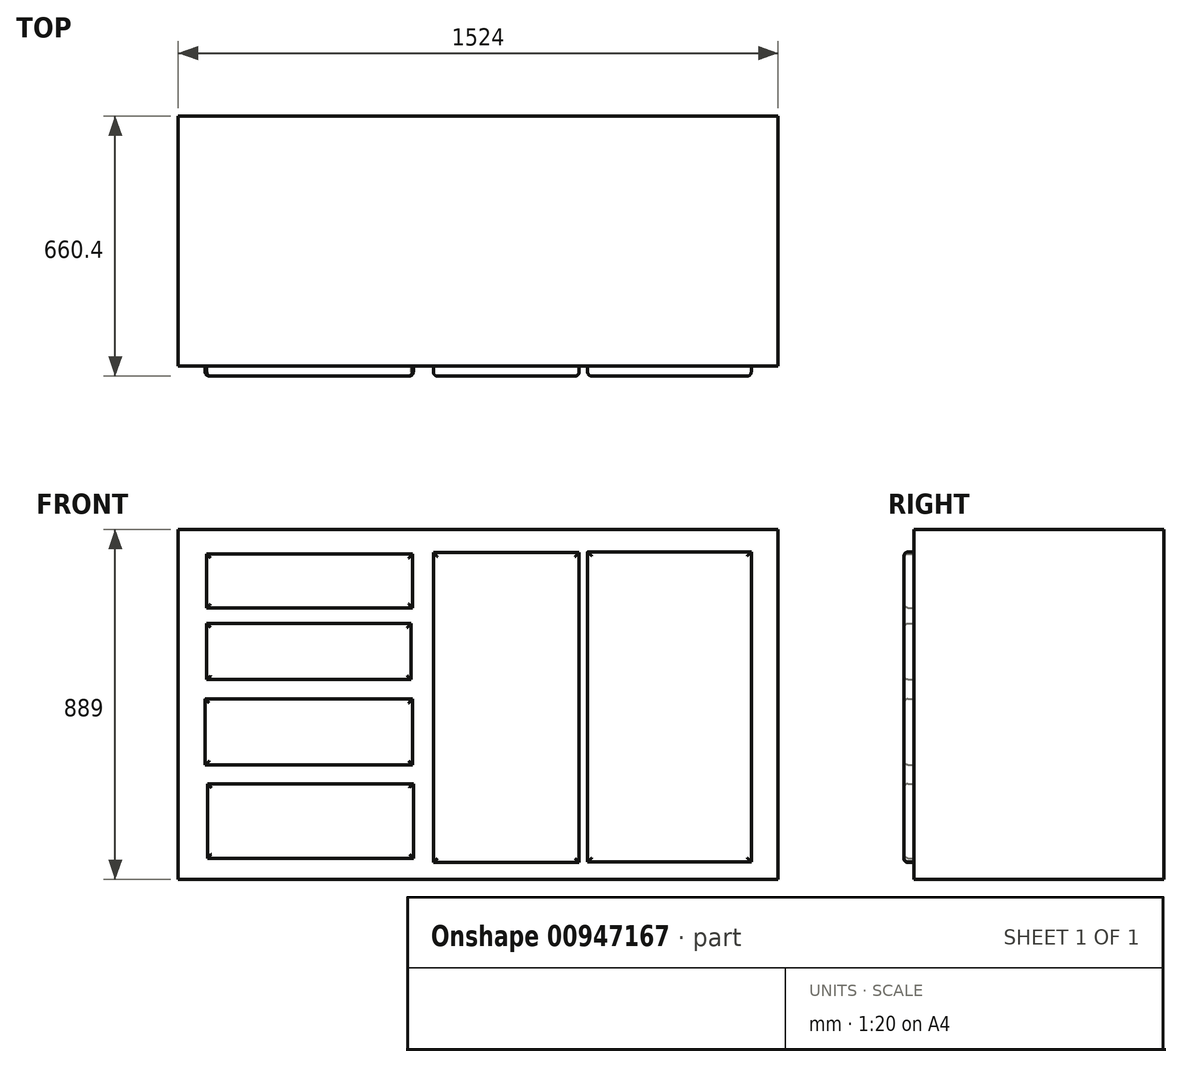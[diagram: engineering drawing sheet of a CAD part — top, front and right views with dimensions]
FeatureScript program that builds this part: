
annotation { "Feature Type Name" : "Feature", "Feature Type Description" : "" }
export const myFeature = defineFeature(function(context is Context, id is Id, definition is map)
    precondition{}
    {
        {
            var Q0;
            Q0=qCreatedBy(makeId("Top.planeOp"),FACE);
            var sketch = newSketch(context, id + "F0", { "sketchPlane" : qUnion([Q0])});
            skLineSegment(sketch, "E0.bottom", {"start": v(0, 0) * mm, "end": v(1524, 0) * mm});
            skLineSegment(sketch, "E0.top", {"start": v(0, 635) * mm, "end": v(1524, 635) * mm});
            skLineSegment(sketch, "E0.left", {"start": v(0, 0) * mm, "end": v(0, 635) * mm});
            skLineSegment(sketch, "E0.right", {"start": v(1524, 0) * mm, "end": v(1524, 635) * mm});
            skSolve(sketch);
        }
        {
            var Q0;
            Q0 = qSketchRegion(id + "F0", true);
            extrude(context, id + "F1", {"entities" : qUnion([Q0]), "depth" : 889 * mm, "offsetDistance" : 25.4 * mm});
        }
        {
            var Q0;
            Q0=makeQuery(id+"F1.opExtrude","SWEPT_FACE",FACE,{"disambiguationData":[OSD([sQuery(id+"F0.wireOp",EDGE,"E0.bottom")])]});
            var sketch = newSketch(context, id + "F2", { "sketchPlane" : qUnion([Q0])});
            skLineSegment(sketch, "E1.bottom", {"start": v(1455.74, 832.02) * mm, "end": v(1040.15, 832.02) * mm});
            skLineSegment(sketch, "E1.top", {"start": v(1455.74, 44.58) * mm, "end": v(1040.15, 44.58) * mm});
            skLineSegment(sketch, "E1.left", {"start": v(1455.74, 832.02) * mm, "end": v(1455.74, 44.58) * mm});
            skLineSegment(sketch, "E1.right", {"start": v(1040.15, 832.02) * mm, "end": v(1040.15, 44.58) * mm});
            skLineSegment(sketch, "E2.bottom", {"start": v(1018.28, 42.76) * mm, "end": v(648.26, 42.76) * mm});
            skLineSegment(sketch, "E2.top", {"start": v(1018.28, 830.2) * mm, "end": v(648.26, 830.2) * mm});
            skLineSegment(sketch, "E2.left", {"start": v(1018.28, 42.76) * mm, "end": v(1018.28, 830.2) * mm});
            skLineSegment(sketch, "E2.right", {"start": v(648.26, 42.76) * mm, "end": v(648.26, 830.2) * mm});
            skLineSegment(sketch, "E3.bottom", {"start": v(595.4, 826.55) * mm, "end": v(72.26, 826.55) * mm});
            skLineSegment(sketch, "E3.top", {"start": v(595.4, 689.84) * mm, "end": v(72.26, 689.84) * mm});
            skLineSegment(sketch, "E3.left", {"start": v(595.4, 826.55) * mm, "end": v(595.4, 689.84) * mm});
            skLineSegment(sketch, "E3.right", {"start": v(72.26, 826.55) * mm, "end": v(72.26, 689.84) * mm});
            skLineSegment(sketch, "E4.bottom", {"start": v(591.75, 649.74) * mm, "end": v(72.26, 649.74) * mm});
            skLineSegment(sketch, "E4.top", {"start": v(591.75, 507.56) * mm, "end": v(72.26, 507.56) * mm});
            skLineSegment(sketch, "E4.left", {"start": v(591.75, 649.74) * mm, "end": v(591.75, 507.56) * mm});
            skLineSegment(sketch, "E4.right", {"start": v(72.26, 649.74) * mm, "end": v(72.26, 507.56) * mm});
            skLineSegment(sketch, "E5.bottom", {"start": v(595.4, 458.35) * mm, "end": v(68.61, 458.35) * mm});
            skLineSegment(sketch, "E5.top", {"start": v(595.4, 290.65) * mm, "end": v(68.61, 290.65) * mm});
            skLineSegment(sketch, "E5.left", {"start": v(595.4, 458.35) * mm, "end": v(595.4, 290.65) * mm});
            skLineSegment(sketch, "E5.right", {"start": v(68.61, 458.35) * mm, "end": v(68.61, 290.65) * mm});
            skLineSegment(sketch, "E6.bottom", {"start": v(597.22, 243.26) * mm, "end": v(74.08, 243.26) * mm});
            skLineSegment(sketch, "E6.top", {"start": v(597.22, 53.7) * mm, "end": v(74.08, 53.7) * mm});
            skLineSegment(sketch, "E6.left", {"start": v(597.22, 243.26) * mm, "end": v(597.22, 53.7) * mm});
            skLineSegment(sketch, "E6.right", {"start": v(74.08, 243.26) * mm, "end": v(74.08, 53.7) * mm});
            skSolve(sketch);
        }
        {
            var Q0;
            Q0 = qSketchRegion(id + "F2", true);
            extrude(context, id + "F3", {"entities" : qUnion([Q0]), "operationType" : NewBodyOperationType.ADD, "depth" : 25.4 * mm, "offsetDistance" : 25.4 * mm});
        }
        {
            var Q0;
            Q0=makeQuery(id+"F3.opExtrude","CAP_FACE",FACE,{"disambiguationData":[OSD([sQuery(id+"F2.wireOp",EDGE,"E3.bottom"),sQuery(id+"F2.wireOp",EDGE,"E3.top"),sQuery(id+"F2.wireOp",EDGE,"E3.left"),sQuery(id+"F2.wireOp",EDGE,"E3.right")])],"isStart":false});
            var Q1;
            Q1=makeQuery(id+"F3.opExtrude","CAP_FACE",FACE,{"disambiguationData":[OSD([sQuery(id+"F2.wireOp",EDGE,"E2.bottom"),sQuery(id+"F2.wireOp",EDGE,"E2.top"),sQuery(id+"F2.wireOp",EDGE,"E2.left"),sQuery(id+"F2.wireOp",EDGE,"E2.right")])],"isStart":false});
            var Q2;
            Q2=makeQuery(id+"F3.opExtrude","CAP_FACE",FACE,{"disambiguationData":[OSD([sQuery(id+"F2.wireOp",EDGE,"E1.bottom"),sQuery(id+"F2.wireOp",EDGE,"E1.top"),sQuery(id+"F2.wireOp",EDGE,"E1.left"),sQuery(id+"F2.wireOp",EDGE,"E1.right")])],"isStart":false});
            var Q3;
            Q3=makeQuery(id+"F3.opExtrude","CAP_FACE",FACE,{"disambiguationData":[OSD([sQuery(id+"F2.wireOp",EDGE,"E4.bottom"),sQuery(id+"F2.wireOp",EDGE,"E4.top"),sQuery(id+"F2.wireOp",EDGE,"E4.left"),sQuery(id+"F2.wireOp",EDGE,"E4.right")])],"isStart":false});
            var Q4;
            Q4=makeQuery(id+"F3.opExtrude","CAP_FACE",FACE,{"disambiguationData":[OSD([sQuery(id+"F2.wireOp",EDGE,"E5.bottom"),sQuery(id+"F2.wireOp",EDGE,"E5.top"),sQuery(id+"F2.wireOp",EDGE,"E5.left"),sQuery(id+"F2.wireOp",EDGE,"E5.right")])],"isStart":false});
            var Q5;
            Q5=makeQuery(id+"F3.opExtrude","CAP_FACE",FACE,{"disambiguationData":[OSD([sQuery(id+"F2.wireOp",EDGE,"E6.bottom"),sQuery(id+"F2.wireOp",EDGE,"E6.top"),sQuery(id+"F2.wireOp",EDGE,"E6.left"),sQuery(id+"F2.wireOp",EDGE,"E6.right")])],"isStart":false});
            fillet(context, id + "F4", {"entities" : qUnion([Q0, Q1, Q2, Q3, Q4, Q5]), "radius" : 10.16 * mm, "tangentPropagation" : true, "allowEdgeOverflow" : false});
        }
    });
